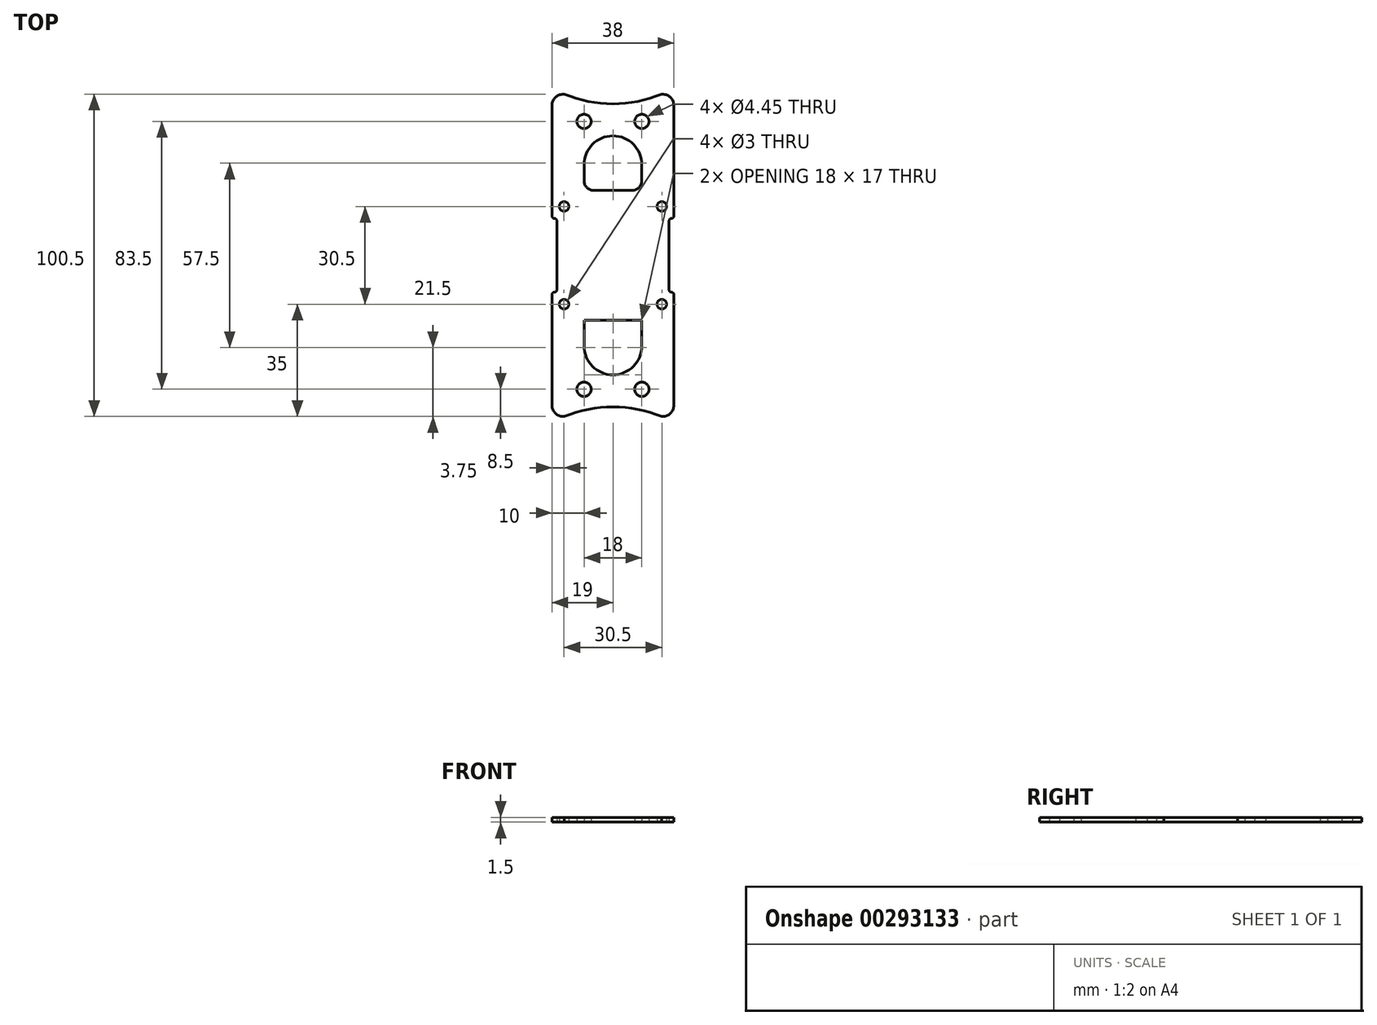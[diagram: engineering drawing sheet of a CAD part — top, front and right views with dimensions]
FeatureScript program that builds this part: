
annotation { "Feature Type Name" : "Feature", "Feature Type Description" : "" }
export const myFeature = defineFeature(function(context is Context, id is Id, definition is map)
    precondition{}
    {
        {
            var Q0;
            Q0=qCreatedBy(makeId("Top.planeOp"),FACE);
            var sketch = newSketch(context, id + "F0", { "sketchPlane" : qUnion([Q0])});
            skLineSegment(sketch, "E0", {"start": v(19, -46.75) * mm, "end": v(19, -12.25) * mm});
            skArc(sketch, "E1", {"start": v(19, -12.25) * mm, "mid": v(18.78, -11.72) * mm, "end": v(18.25, -11.5) * mm});
            skArc(sketch, "E2", {"start": v(17.5, -10.75) * mm, "mid": v(17.72, -11.28) * mm, "end": v(18.25, -11.5) * mm});
            skLineSegment(sketch, "E3", {"start": v(17.5, -10.75) * mm, "end": v(17.5, 10.75) * mm});
            skArc(sketch, "E4", {"start": v(18.25, 11.5) * mm, "mid": v(17.72, 11.28) * mm, "end": v(17.5, 10.75) * mm});
            skArc(sketch, "E5", {"start": v(18.25, 11.5) * mm, "mid": v(18.78, 11.72) * mm, "end": v(19, 12.25) * mm});
            skLineSegment(sketch, "E6", {"start": v(19, 12.25) * mm, "end": v(19, 46.75) * mm});
            skArc(sketch, "E7", {"start": v(19, 46.75) * mm, "mid": v(17.97, 49.22) * mm, "end": v(15.5, 50.25) * mm});
            skLineSegment(sketch, "E8", {"start": v(15.5, 50.25) * mm, "end": v(15.17, 50.25) * mm});
            skArc(sketch, "E9", {"start": v(-15.17, 50.25) * mm, "mid": v(0, 47.25) * mm, "end": v(15.17, 50.25) * mm});
            skLineSegment(sketch, "E10", {"start": v(-15.17, 50.25) * mm, "end": v(-15.5, 50.25) * mm});
            skArc(sketch, "E11", {"start": v(-15.5, 50.25) * mm, "mid": v(-17.97, 49.22) * mm, "end": v(-19, 46.75) * mm});
            skLineSegment(sketch, "E12", {"start": v(-19, 46.75) * mm, "end": v(-19, 12.25) * mm});
            skArc(sketch, "E13", {"start": v(-19, 12.25) * mm, "mid": v(-18.78, 11.72) * mm, "end": v(-18.25, 11.5) * mm});
            skArc(sketch, "E14", {"start": v(-17.5, 10.75) * mm, "mid": v(-17.72, 11.28) * mm, "end": v(-18.25, 11.5) * mm});
            skLineSegment(sketch, "E15", {"start": v(-17.5, 10.75) * mm, "end": v(-17.5, -10.75) * mm});
            skArc(sketch, "E16", {"start": v(-18.25, -11.5) * mm, "mid": v(-17.72, -11.28) * mm, "end": v(-17.5, -10.75) * mm});
            skArc(sketch, "E17", {"start": v(-18.25, -11.5) * mm, "mid": v(-18.78, -11.72) * mm, "end": v(-19, -12.25) * mm});
            skLineSegment(sketch, "E18", {"start": v(-19, -12.25) * mm, "end": v(-19, -46.75) * mm});
            skArc(sketch, "E19", {"start": v(-19, -46.75) * mm, "mid": v(-17.97, -49.22) * mm, "end": v(-15.5, -50.25) * mm});
            skLineSegment(sketch, "E20", {"start": v(-15.5, -50.25) * mm, "end": v(-15.17, -50.25) * mm});
            skArc(sketch, "E21", {"start": v(15.17, -50.25) * mm, "mid": v(0, -47.25) * mm, "end": v(-15.17, -50.25) * mm});
            skLineSegment(sketch, "E22", {"start": v(15.17, -50.25) * mm, "end": v(15.5, -50.25) * mm});
            skArc(sketch, "E23", {"start": v(15.5, -50.25) * mm, "mid": v(17.97, -49.22) * mm, "end": v(19, -46.75) * mm});
            skCircle(sketch, "E24", {"center": v(9, -41.75) * mm, "radius": 2.23 * mm});
            skCircle(sketch, "E25", {"center": v(-9, -41.75) * mm, "radius": 2.23 * mm});
            skCircle(sketch, "E26", {"center": v(9, 41.75) * mm, "radius": 2.23 * mm});
            skCircle(sketch, "E27", {"center": v(-9, 41.75) * mm, "radius": 2.23 * mm});
            skCircle(sketch, "E28", {"center": v(15.25, -15.25) * mm, "radius": 1.5 * mm});
            skCircle(sketch, "E29", {"center": v(-15.25, -15.25) * mm, "radius": 1.5 * mm});
            skCircle(sketch, "E30", {"center": v(15.25, 15.25) * mm, "radius": 1.5 * mm});
            skCircle(sketch, "E31", {"center": v(-15.25, 15.25) * mm, "radius": 1.5 * mm});
            skLineSegment(sketch, "E32", {"start": v(9, -20.25) * mm, "end": v(9, -28.25) * mm});
            skLineSegment(sketch, "E33", {"start": v(-9, -20.25) * mm, "end": v(9, -20.25) * mm});
            skLineSegment(sketch, "E34", {"start": v(-9, -28.25) * mm, "end": v(-9, -20.25) * mm});
            skArc(sketch, "E35", {"start": v(-9, -28.25) * mm, "mid": v(0, -37.25) * mm, "end": v(9, -28.25) * mm});
            skArc(sketch, "E36", {"start": v(6, 20.25) * mm, "mid": v(8.12, 21.13) * mm, "end": v(9, 23.25) * mm});
            skLineSegment(sketch, "E37", {"start": v(-6, 20.25) * mm, "end": v(6, 20.25) * mm});
            skArc(sketch, "E38", {"start": v(-9, 23.25) * mm, "mid": v(-8.12, 21.13) * mm, "end": v(-6, 20.25) * mm});
            skLineSegment(sketch, "E39", {"start": v(-9, 28.25) * mm, "end": v(-9, 23.25) * mm});
            skArc(sketch, "E40", {"start": v(9, 28.25) * mm, "mid": v(0, 37.25) * mm, "end": v(-9, 28.25) * mm});
            skLineSegment(sketch, "E41", {"start": v(9, 23.25) * mm, "end": v(9, 28.25) * mm});
            skSolve(sketch);
        }
        {
            var Q0;
            Q0 = qSketchRegion(id + "F0", true);
            extrude(context, id + "F1", {"entities" : qUnion([Q0]), "depth" : 1.5 * mm});
        }
    });
